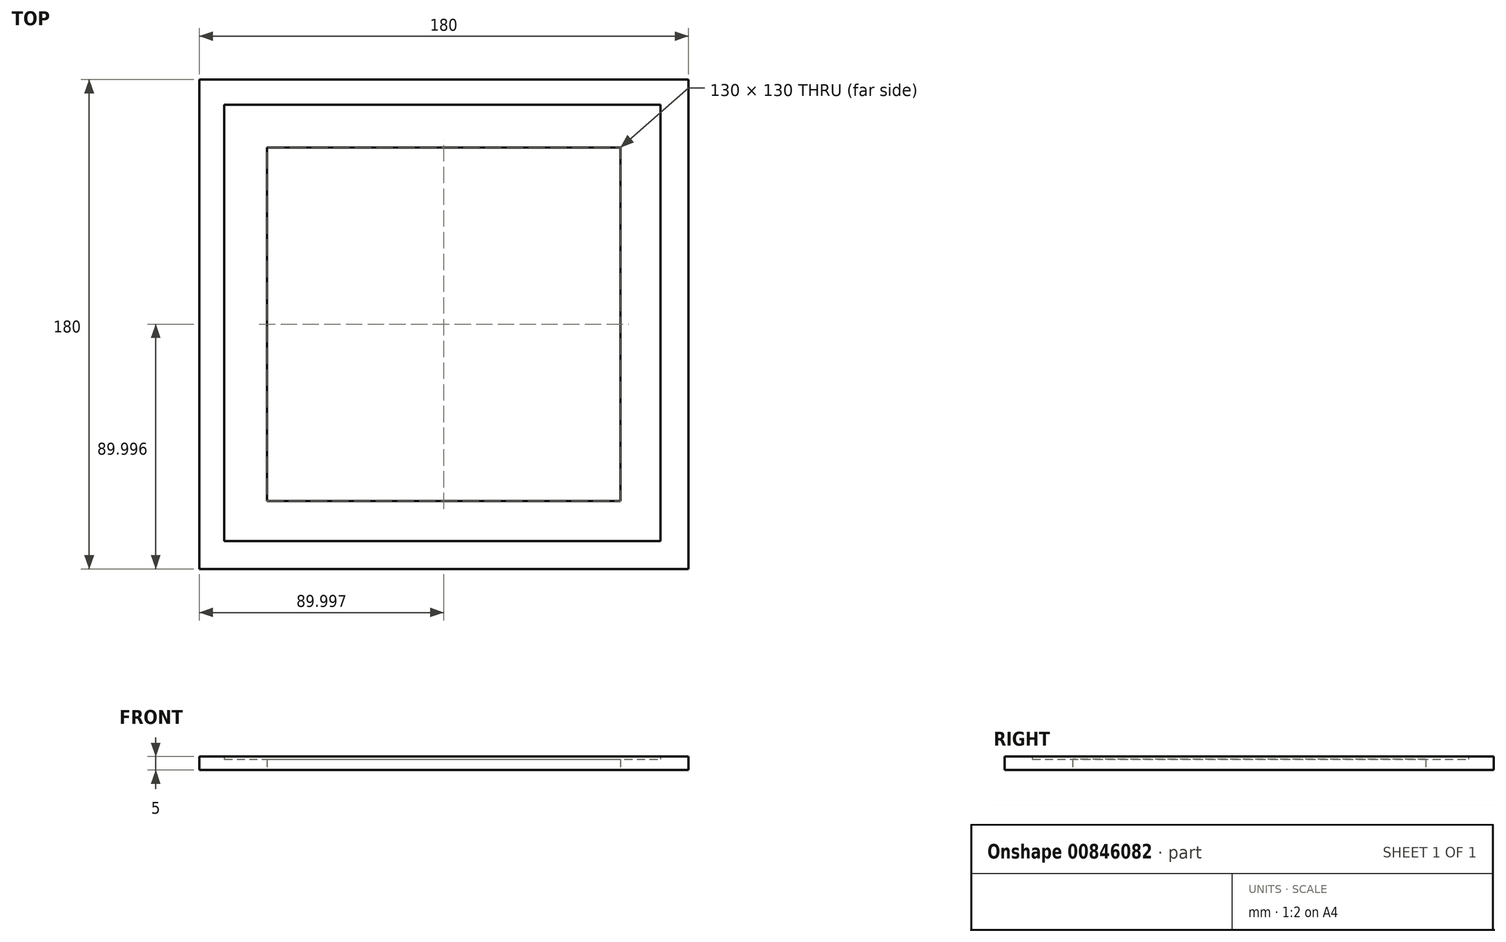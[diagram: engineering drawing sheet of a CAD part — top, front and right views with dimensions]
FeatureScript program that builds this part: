
annotation { "Feature Type Name" : "Feature", "Feature Type Description" : "" }
export const myFeature = defineFeature(function(context is Context, id is Id, definition is map)
    precondition{}
    {
        {
            var Q0;
            Q0=qCreatedBy(makeId("Top.planeOp"),FACE);
            var sketch = newSketch(context, id + "F0", { "sketchPlane" : qUnion([Q0])});
            skLineSegment(sketch, "E0.bottom", {"start": v(-93.8, 126.6) * mm, "end": v(86.2, 126.6) * mm});
            skLineSegment(sketch, "E0.top", {"start": v(-93.8, -53.4) * mm, "end": v(86.2, -53.4) * mm});
            skLineSegment(sketch, "E0.left", {"start": v(-93.8, 126.6) * mm, "end": v(-93.8, -53.4) * mm});
            skLineSegment(sketch, "E0.right", {"start": v(86.2, 126.6) * mm, "end": v(86.2, -53.4) * mm});
            skLineSegment(sketch, "E1.bottom", {"start": v(-68.8, 101.6) * mm, "end": v(61.2, 101.6) * mm});
            skLineSegment(sketch, "E1.top", {"start": v(-68.8, -28.4) * mm, "end": v(61.2, -28.4) * mm});
            skLineSegment(sketch, "E1.left", {"start": v(-68.8, 101.6) * mm, "end": v(-68.8, -28.4) * mm});
            skLineSegment(sketch, "E1.right", {"start": v(61.2, 101.6) * mm, "end": v(61.2, -28.4) * mm});
            skSolve(sketch);
        }
        {
            var Q0;
            Q0 = qSketchRegion(id + "F0", true);
            extrude(context, id + "F1", {"entities" : qUnion([Q0]), "depth" : 4 * mm, "offsetDistance" : 25 * mm});
        }
        {
            var Q0;
            Q0=makeQuery(id+"F1.opExtrude","CAP_FACE",FACE,{"disambiguationData":[OSD([sQuery(id+"F0.wireOp",EDGE,"E0.bottom"),sQuery(id+"F0.wireOp",EDGE,"E0.top"),sQuery(id+"F0.wireOp",EDGE,"E0.left"),sQuery(id+"F0.wireOp",EDGE,"E0.right"),sQuery(id+"F0.wireOp",EDGE,"E1.bottom"),sQuery(id+"F0.wireOp",EDGE,"E1.top"),sQuery(id+"F0.wireOp",EDGE,"E1.left"),sQuery(id+"F0.wireOp",EDGE,"E1.right")])],"isStart":false});
            var sketch = newSketch(context, id + "F2", { "sketchPlane" : qUnion([Q0])});
            skLineSegment(sketch, "E2.bottom", {"start": v(-93.8, -53.4) * mm, "end": v(86.2, -53.4) * mm});
            skLineSegment(sketch, "E2.top", {"start": v(-93.8, 126.6) * mm, "end": v(86.2, 126.6) * mm});
            skLineSegment(sketch, "E2.left", {"start": v(-93.8, -53.4) * mm, "end": v(-93.8, 126.6) * mm});
            skLineSegment(sketch, "E2.right", {"start": v(86.2, -53.4) * mm, "end": v(86.2, 126.6) * mm});
            skLineSegment(sketch, "E3.bottom", {"start": v(-84.54, -43.15) * mm, "end": v(75.96, -43.15) * mm});
            skLineSegment(sketch, "E3.top", {"start": v(-84.54, 117.35) * mm, "end": v(75.96, 117.35) * mm});
            skLineSegment(sketch, "E3.left", {"start": v(-84.54, -43.15) * mm, "end": v(-84.54, 117.35) * mm});
            skLineSegment(sketch, "E3.right", {"start": v(75.96, -43.15) * mm, "end": v(75.96, 117.35) * mm});
            skSolve(sketch);
        }
        {
            var Q0;
            Q0=makeQuery(id+"F2.imprint","IMPRINT",FACE,{"disambiguationData":[TD([[makeQuery(id+"F2.imprint","IMPRINT",EDGE,{"derivedFrom":sQuery(id+"F2.wireOp",EDGE,"E2.bottom")}),1.0]])]});
            extrude(context, id + "F3", {"entities" : qUnion([Q0]), "operationType" : NewBodyOperationType.ADD, "depth" : 1 * mm, "offsetDistance" : 25 * mm});
        }
    });
